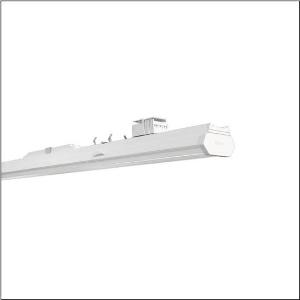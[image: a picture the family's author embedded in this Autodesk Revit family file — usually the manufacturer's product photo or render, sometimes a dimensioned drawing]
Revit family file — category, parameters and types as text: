
# Revit family: licross_21_protected_ho_52td12dn4e5m3c
name_source: partatom
category: Lighting Fixtures
units: mm (PartAtom-declared; Revit-internal decimal feet)

## family parameters
Cut with Voids When Loaded = No
Host = Face
Light Source = No
Part Type = Normal
Room Calculation Point = No
Round Connector Dimension = Use Diameter
Shared = No

## types (1)
- --- (1 x LED, 910 lm, 7.6 W, 4000K)
    Apparent Load = 8 VA
    CIE Flux Codes = 70 91 97 98 100
    Color Rendering = 80
    Color Temperature = 4000K
    Default Elevation = 1800 mm
    Description = Licross 21 Protected HO, luminaire insert, of sheet steel, galvanised, coil coated, white, length: 1.500mm, width: 90mm, height: 103mm, LED rated luminous flux: 14.690lm, light colour: 840, SDCM (Standard Deviation of Colour Matching)MacAdam ≤ 3 SDCM (initial), control gear: DALI 2 (for two DALI lines), with plug, 6-pole, with phase selection, for trunking rail, 14-core, mains connection: 220..240V, AC, 50/60Hz, rated input power: 89W, for trunking rail, 14-core, internal wiring halogen-free, for emergency light function, converter,control gear: single battery element, battery: LiFePO4, 9Ah, primary light control with lens, of plastic, primary optical cover: cover, of PMMA, light emission: direct distribution, primary light characteristic: symmetric, protection rating (complete): IP54, insulation class (complete): insulation class I (protective earthing), certification: CE, UKCA, protection symbol: D if used in an environment with non-conductive dust loads with corresponding accessories, impact resistance: IK06, permissible ambient temperature for indoor applications: +5..+30°C, standard: EN 60598-2-22, LABS conformity tested according to VDMA 24364:2018-05, reducing of maximum allowable ambient temperature of 5°C with ceiling mounting, corresponds to IFS (International Featured Standards) requirements for safety and quality in the food industry, The light source and the operating device comply with the requirements of the Ecodesign Regulation (EU) 2019/2020 and are replaceable in accordance with this regulation, packaging unit: 1 piece
    Height = 92 mm
    Lamp = 1 x LED
    Lamp Light Flux = 910 lm
    Lamp Power = 7.6 W
    Lamp count = 1
    Length = 1500 mm
    Luminous efficacy = 120 lm/W
    Manufacturer = Siteco
    ModVariant = No
    Model = 52TD12DN4E5M3C
    Mounting Place = Ceiling
    Mounting Type = Pendant
    Number of Poles = 1
    OnlyDefault = Yes
    Power Factor = 1
    Product Name = Licross 21 Protected HO
    Product group = luminaire insert | ceiling pendant
    ProductGroupID = 901
    Protection Class = Protection class I
    Protection Degree = IP 54
    RLX_Detail_Level = 1
    RLX_Emergency_Light_Flux = 0 lm
    RLX_Emergency_Type = 0
    RLX_Emergency_Type_DB = No
    RlxData = <blob elided: 25105 chars, md5=04ba4130>
    Socket = socket
    Standby Power = 0 W
    System Light Flux = 910 lm
    System Power = 8 W
    Type Comments = : emergency light operation: 3 h
    Type Image = l_1256148.jpg
    URL = http://relux.com
    VarID = @adj_112731
    Voltage = 0 V
    Weight = 0.00 kg
    Width = 88 mm

## geometry (parser evidence)
native form markers: Blend x4, Sweep x9
no freeform markers — native parametric forms only
